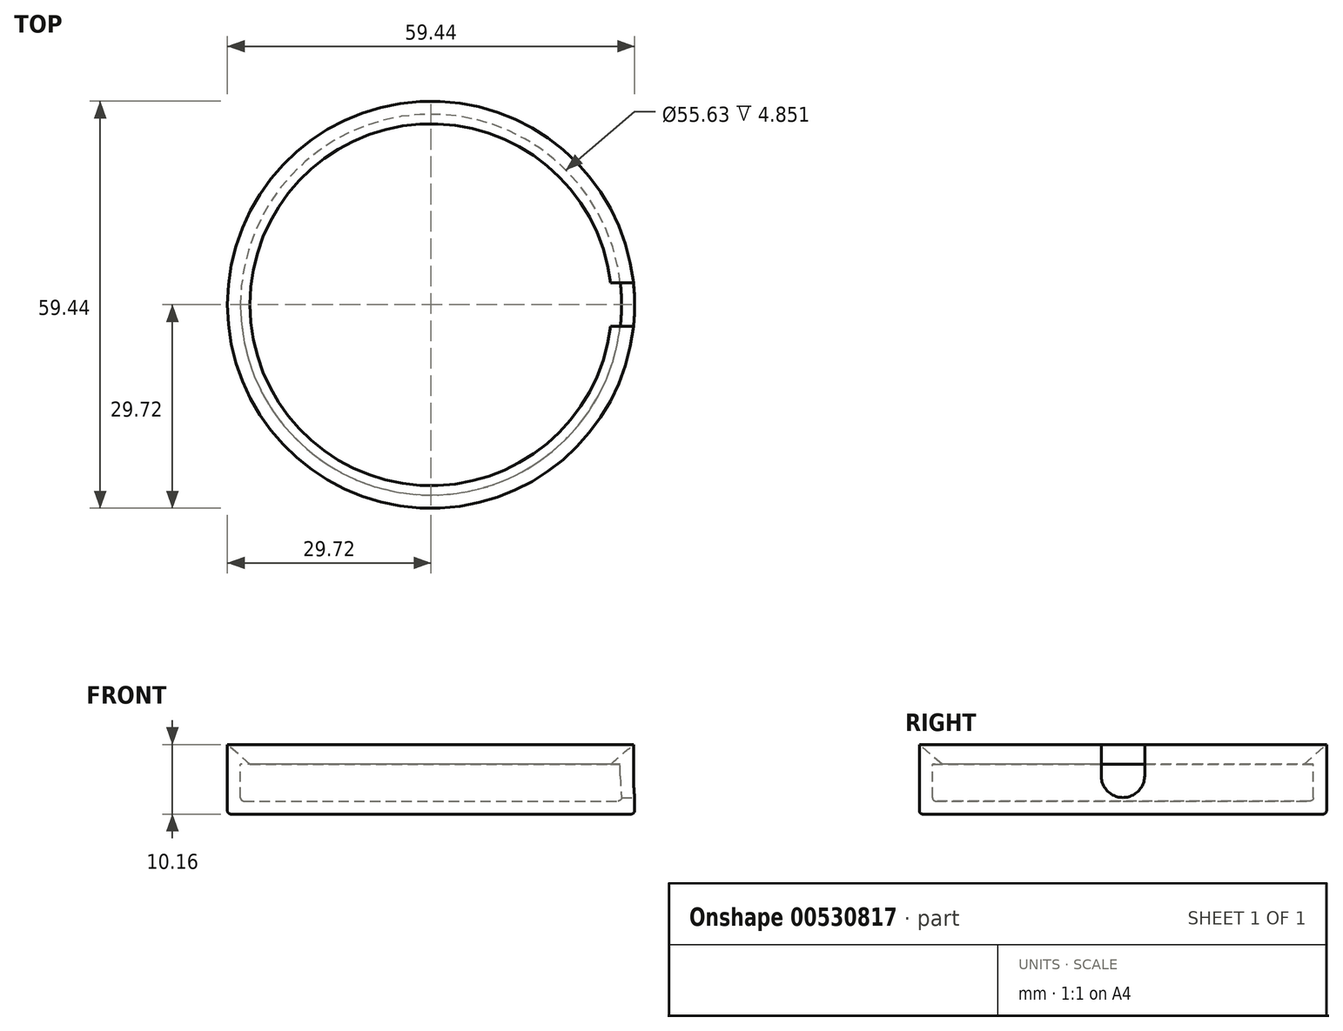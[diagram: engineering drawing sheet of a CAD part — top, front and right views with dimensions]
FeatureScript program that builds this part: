
annotation { "Feature Type Name" : "Feature", "Feature Type Description" : "" }
export const myFeature = defineFeature(function(context is Context, id is Id, definition is map)
    precondition{}
    {
        {
            var Q0;
            Q0=qCreatedBy(makeId("Top.planeOp"),FACE);
            var sketch = newSketch(context, id + "F0", { "sketchPlane" : qUnion([Q0])});
            skCircle(sketch, "E0", {"center": v(0, 0) * mm, "radius": 29.72 * mm});
            skSolve(sketch);
        }
        {
            var Q0;
            Q0=makeQuery(id+"F0.imprint","IMPRINT",FACE,{"disambiguationData":[TD([[makeQuery(id+"F0.imprint","IMPRINT",EDGE,{"derivedFrom":sQuery(id+"F0.wireOp",EDGE,"E0")}),1.0]])]});
            extrude(context, id + "F1", {"entities" : qUnion([Q0]), "depth" : 10.16 * mm, "offsetDistance" : 25.4 * mm});
        }
        {
            var Q0;
            Q0=qCreatedBy(makeId("Front.planeOp"),FACE);
            var sketch = newSketch(context, id + "F2", { "sketchPlane" : qUnion([Q0])});
            skLineSegment(sketch, "E1.0", {"start": v(-29.72, 10.16) * mm, "end": v(29.72, 10.16) * mm});
            skLineSegment(sketch, "E2", {"start": v(26.42, 7.26) * mm, "end": v(29.72, 10.16) * mm});
            skLineSegment(sketch, "E3", {"start": v(26.42, 7.26) * mm, "end": v(0, 7.26) * mm});
            skLineSegment(sketch, "E4", {"start": v(0, 7.26) * mm, "end": v(0, 10.16) * mm});
            skSolve(sketch);
        }
        {
            var Q0;
            Q0 = qSketchRegion(id + "F2", true);
            var Q1;
            Q1=sQuery(id+"F2.wireOp",EDGE,"E4");
            revolve(context, id + "F3", {"operationType" : NewBodyOperationType.REMOVE, "entities" : qUnion([Q0]), "axis" : qUnion([Q1]), "revolveType" : RevolveType.FULL});
        }
        {
            var Q0;
            Q0=qCreatedBy(makeId("Front.planeOp"),FACE);
            var sketch = newSketch(context, id + "F4", { "sketchPlane" : qUnion([Q0])});
            skLineSegment(sketch, "E5.0.0", {"start": v(-26.42, 7.26) * mm, "end": v(0, 7.26) * mm});
            skLineSegment(sketch, "E6", {"start": v(-26.42, 7.26) * mm, "end": v(-27.81, 7.26) * mm});
            skLineSegment(sketch, "E7", {"start": v(-27.81, 7.26) * mm, "end": v(-27.81, 1.9) * mm});
            skLineSegment(sketch, "E8", {"start": v(-27.81, 1.9) * mm, "end": v(0, 1.9) * mm});
            skLineSegment(sketch, "E9", {"start": v(0, 1.9) * mm, "end": v(0, 7.26) * mm});
            skPoint(sketch, "E10.orphan", {"position": v(26.42, 7.26) * mm});
            skLineSegment(sketch, "E11", {"start": v(-29.72, 0) * mm, "end": v(-29.72, 7.62) * mm, "construction": true});
            skLineSegment(sketch, "E12", {"start": v(29.72, 7.62) * mm, "end": v(29.72, 0) * mm, "construction": true});
            skSolve(sketch);
        }
        {
            var Q0;
            Q0 = qSketchRegion(id + "F4", true);
            var Q1;
            Q1=sQuery(id+"F4.wireOp",EDGE,"E9");
            revolve(context, id + "F5", {"operationType" : NewBodyOperationType.REMOVE, "entities" : qUnion([Q0]), "axis" : qUnion([Q1]), "revolveType" : RevolveType.FULL, "oppositeDirection" : true});
        }
        {
            var Q0;
            Q0=makeQuery(id+"F5.boolean.opBoolean","COPY",FACE,{"derivedFrom":makeQuery(id+"F5.opRevolve","SWEPT_FACE",FACE,{"disambiguationData":[OSD([sQuery(id+"F4.wireOp",EDGE,"E8")])]})});
            var Q1;
            Q1=makeQuery(id+"F1.opExtrude","CAP_EDGE",EDGE,{"disambiguationData":[OSD([sQuery(id+"F0.wireOp",EDGE,"E0")])],"isStart":true});
            fillet(context, id + "F6", {"entities" : qUnion([Q0, Q1]), "radius" : 0.5 * mm, "tangentPropagation" : true, "allowEdgeOverflow" : false});
        }
        {
            var Q0;
            Q0=makeQuery(id+"F9.boolean.opBoolean","MERGE",FACE,{"derivedFrom":[makeQuery(id+"F5.boolean.opBoolean","COPY",FACE,{"derivedFrom":makeQuery(id+"F5.opRevolve","SWEPT_FACE",FACE,{"disambiguationData":[OSD([sQuery(id+"F4.wireOp",EDGE,"E8")])]})}),makeQuery(id+"F9.opExtrude","CAP_FACE",FACE,{"disambiguationData":[OSD([sQuery(id+"F8.wireOp",EDGE,"E13.bottom"),sQuery(id+"F8.wireOp",EDGE,"E13.top"),sQuery(id+"F8.wireOp",EDGE,"E13.left"),sQuery(id+"F8.wireOp",EDGE,"E13.right")])],"isStart":true})]});
            cPlane(context, id + "F7", {"entities" : qUnion([Q0]), "cplaneType" : CPlaneType.OFFSET, "offset" : 0.5 * mm, "width" : 152.4 * mm, "height" : 152.4 * mm});
        }
        {
            var Q0;
            Q0=qCreatedBy(id+"F7.planeOp",FACE);
            var sketch = newSketch(context, id + "F8", { "sketchPlane" : qUnion([Q0])});
            skLineSegment(sketch, "E13.bottom", {"start": v(25.74, 3.18) * mm, "end": v(30.5, 3.18) * mm});
            skLineSegment(sketch, "E13.top", {"start": v(25.74, -3.18) * mm, "end": v(30.5, -3.18) * mm});
            skLineSegment(sketch, "E13.left", {"start": v(25.74, 3.17) * mm, "end": v(25.74, -3.18) * mm});
            skLineSegment(sketch, "E13.right", {"start": v(30.5, 3.17) * mm, "end": v(30.5, -3.18) * mm});
            skSolve(sketch);
        }
        {
            var Q0;
            Q0 = qSketchRegion(id + "F8", true);
            extrude(context, id + "F9", {"entities" : qUnion([Q0]), "operationType" : NewBodyOperationType.REMOVE, "depth" : 25.4 * mm, "offsetDistance" : 25.4 * mm});
        }
        {
            var Q0;
            Q0=makeQuery(id+"F9.boolean.opBoolean","COPY",EDGE,{"derivedFrom":makeQuery(id+"F9.opExtrude","CAP_EDGE",EDGE,{"disambiguationData":[OSD([sQuery(id+"F8.wireOp",EDGE,"E13.bottom")])],"isStart":true})});
            var Q1;
            Q1=makeQuery(id+"F9.boolean.opBoolean","COPY",EDGE,{"derivedFrom":makeQuery(id+"F9.opExtrude","CAP_EDGE",EDGE,{"disambiguationData":[OSD([sQuery(id+"F8.wireOp",EDGE,"E13.top")])],"isStart":true})});
            fillet(context, id + "F10", {"entities" : qUnion([Q0, Q1]), "radius" : 3.17 * mm, "tangentPropagation" : true, "allowEdgeOverflow" : false});
        }
    });
